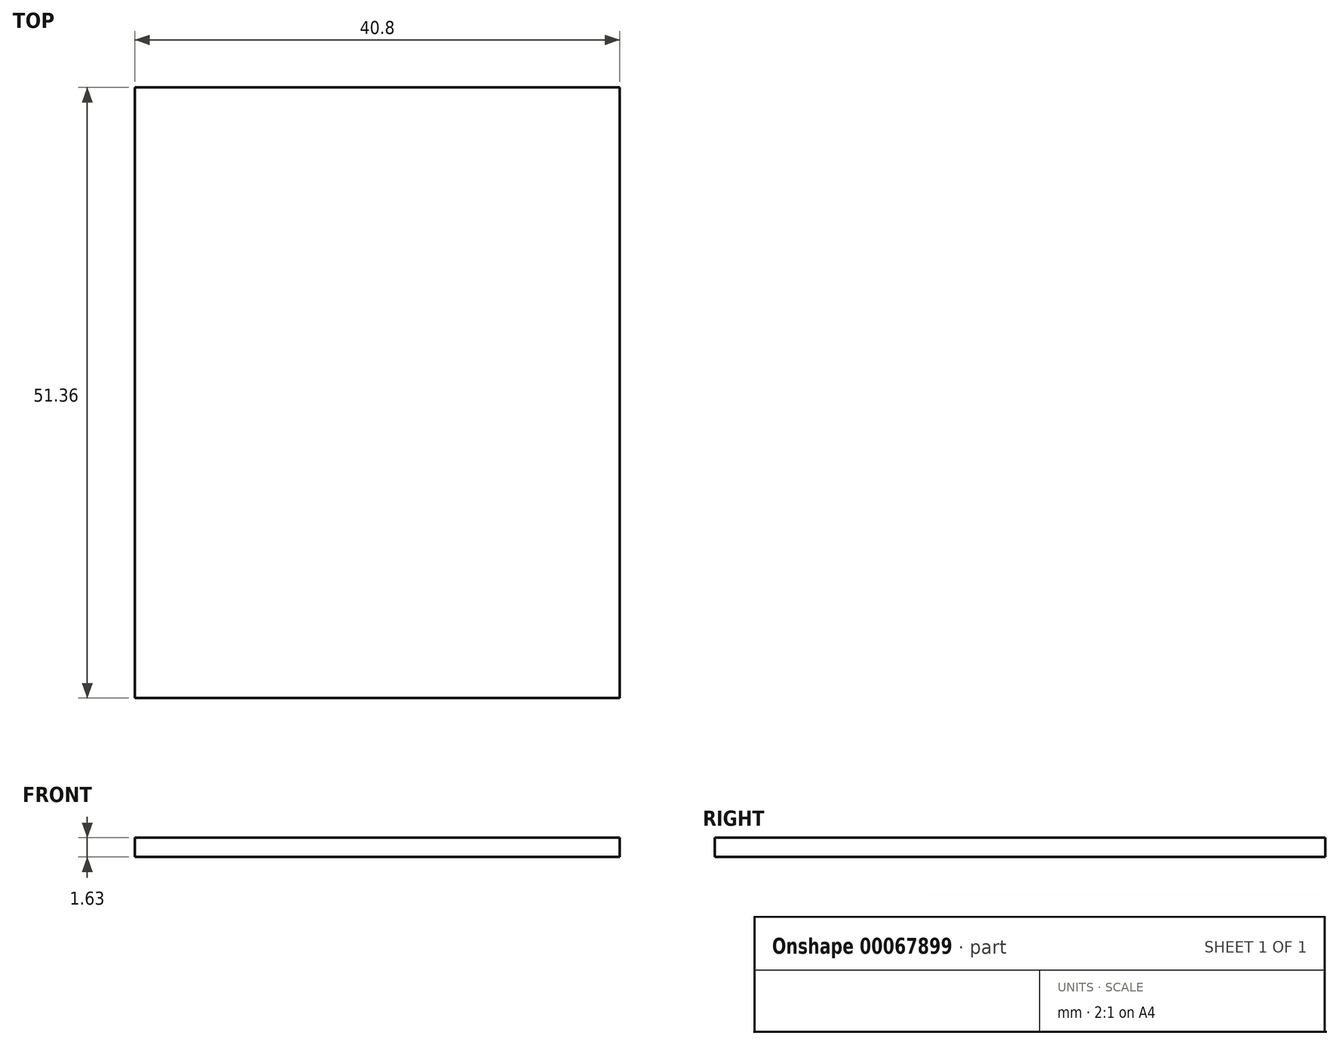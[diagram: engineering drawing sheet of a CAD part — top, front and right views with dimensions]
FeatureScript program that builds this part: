
annotation { "Feature Type Name" : "Feature", "Feature Type Description" : "" }
export const myFeature = defineFeature(function(context is Context, id is Id, definition is map)
    precondition{}
    {
        {
            var Q0;
            Q0=qCreatedBy(makeId("Top.planeOp"),FACE);
            var sketch = newSketch(context, id + "F0", { "sketchPlane" : qUnion([Q0])});
            skLineSegment(sketch, "E0.bottom", {"start": v(20.4, 25.68) * mm, "end": v(-20.4, 25.68) * mm});
            skLineSegment(sketch, "E0.top", {"start": v(20.4, -25.68) * mm, "end": v(-20.4, -25.68) * mm});
            skLineSegment(sketch, "E0.left", {"start": v(20.4, 25.68) * mm, "end": v(20.4, -25.68) * mm});
            skLineSegment(sketch, "E0.right", {"start": v(-20.4, 25.68) * mm, "end": v(-20.4, -25.68) * mm});
            skPoint(sketch, "E0.middle", {"position": v(0, 0) * mm});
            skSolve(sketch);
        }
        {
            var Q0;
            Q0 = qSketchRegion(id + "F0", true);
            extrude(context, id + "F1", {"entities" : qUnion([Q0]), "depth" : 1.63 * mm});
        }
    });
